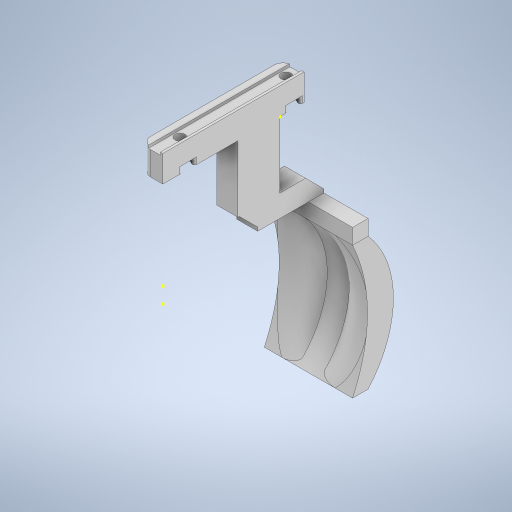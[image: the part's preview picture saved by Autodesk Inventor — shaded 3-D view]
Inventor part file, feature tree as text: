
AUTODESK INVENTOR PART (.ipt)
format: ipt  version: 2024 (Build 280153000, 153)  size: 504,320 bytes
history: native  units: in
note: dims shown in document units (in); Inventor stores cm internally (conversion verified against a paired STEP export)
features: sketch x15, extrude x10, fillet x4, projected_geometry x4, chamfer x2, sweep x1
ambient origin geometry x8: Origin, YZ Plane, XZ Plane, XY Plane, X Axis, Y Axis, Z Axis, Center Point
bodies: Solid1 (feature_tree), Solid4 (feature_tree)
feature tree (36):
  extrude  "Extrusion1"  Depth=2.5197in
  extrude  "Extrusion2"  Depth=1.8898in
  extrude  "Extrusion3"  Depth=0.4724in TaperAngle=0.0deg
  fillet  "Fillet1"  Radius=0.0433in
  fillet  "Fillet2"  Radius=0.2126in
  extrude  "Extrusion19"  Depth=0.4724in TaperAngle=0.0deg
  extrude  "Extrusion21"  Depth=0.1181in TaperAngle=0.0deg
  sketch  "Sketch41"  dims[d17=0.1772in d18=0.0394in]
  extrude  "Extrusion22"  Depth=0.0394in
  chamfer  "Chamfer4"  Distance=1.1811in
  chamfer  "Chamfer5"  Distance=0.3937in
  sketch  "Sketch60"  dims[d76=0.4724in]
  sketch  "Sketch61"  dims[d107=0.102in]
  sweep  "Sweep6"
  extrude  "Extrusion25"  Depth=0.2756in TaperAngle=0.0deg
  extrude  "Extrusion26"  Depth=0.3287in TaperAngle=45.0deg
  extrude  "Extrusion27"  Depth=2.3622in
  fillet  "Fillet17"  Radius=1.5748in
  extrude  "Extrusion28"  TaperAngle=0.0deg  [1 undecoded]
  fillet  "Fillet18"  Radius=3.6688in
  sketch  "Sketch1"  dims[d1=0.374in d2=2.5197in]
  sketch  "Sketch2"  dims[d3=0.1772in d4=1.8898in]
  sketch  "Sketch3"  dims[d6=0.1457in d7=0.4724in d8=0.0in d9=0.0433in d10=0.2126in]
  projected_geometry  "Projected Loop2"
  projected_geometry  "Projected Loop3"
  projected_geometry  "Projected Loop4"
  projected_geometry  "Projected Loop5"
  sketch  "Sketch28"  dims[d11=0.0472in d12=0.4724in d13=0.0in]
  sketch  "Sketch40"  dims[d14=0.2953in d15=0.1181in d16=0.0in]
  sketch  "Sketch42"  dims[d19=0.1575in]
  sketch  "Sketch62"  dims[d108=0.748in d109=1.1811in d110=0.0in]
  sketch  "Sketch63"  dims[d130=0.7874in]
  sketch  "Sketch64"  dims[d131=1.1811in d132=0.3937in d133=0.0in]
  sketch  "Sketch65"  dims[d134=0.7874in d135=0.2756in]
  sketch  "Sketch67"  dims[d137=1.5748in d138=0.2756in d139=0.0in]
  sketch  "Sketch70"  dims[d156=0.3287in d157=0.0787in d158=45.0deg d159=0.3287in d160=0.0787in d161=45.0deg d166=2.3622in d167=1.5748in d168=0.0in d169=0.0in d170=3.6688in d171=0.0in d172=0.3937in d173=0.5374in d174=0.0in d175=0.5906in d176=0.0in d177=0.8268in d178=0.5906in d179=0.0in d180=0.8268in d42=0.0197in d43=0.0344in d44=0.0197in d45=0.0344in d46=0.0in d47=0.0in d48=0.0in d49=0.0in d50=0.0in d51=0.0in d52=0.0in d53=0.0in d55=0.0197in d56=0.0344in d57=0.0197in d58=0.0344in d60=0.0197in d61=0.0344in d62=0.0197in d63=0.0344in d72=0.0197in d73=0.0344in d74=0.0197in d75=0.0344in d140=0.0197in d141=0.0344in]
note: 1 required parameter value undecoded (feature->parameter linkage not recoverable at this tier; creation-order binding heuristic only, values carry confidence <= 0.55)
